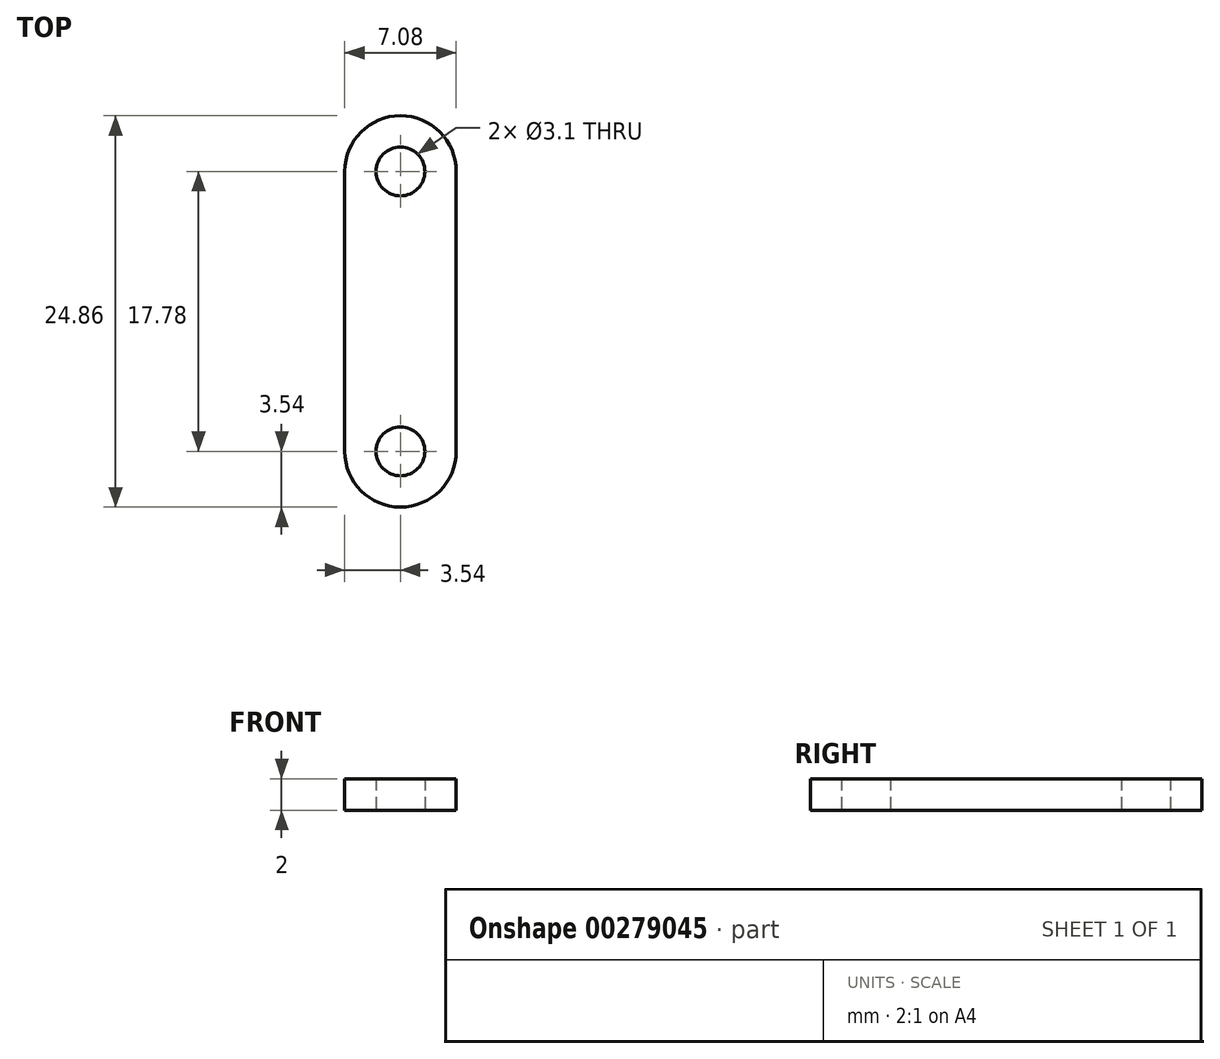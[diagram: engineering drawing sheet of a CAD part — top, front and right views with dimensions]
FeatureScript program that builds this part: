
annotation { "Feature Type Name" : "Feature", "Feature Type Description" : "" }
export const myFeature = defineFeature(function(context is Context, id is Id, definition is map)
    precondition{}
    {
        {
            var Q0;
            Q0=qCreatedBy(makeId("Top.planeOp"),FACE);
            var sketch = newSketch(context, id + "F0", { "sketchPlane" : qUnion([Q0])});
            skLineSegment(sketch, "E0.bottom", {"start": v(0, -12.43) * mm, "end": v(0, -12.43) * mm});
            skLineSegment(sketch, "E0.top", {"start": v(0, 12.43) * mm, "end": v(0, 12.43) * mm});
            skLineSegment(sketch, "E0.left", {"start": v(3.54, -8.9) * mm, "end": v(3.54, 8.9) * mm});
            skLineSegment(sketch, "E0.right", {"start": v(-3.54, -8.89) * mm, "end": v(-3.54, 8.89) * mm});
            skPoint(sketch, "E0.middle", {"position": v(0, 0) * mm});
            skLineSegment(sketch, "E1", {"start": v(-7.16, -8.9) * mm, "end": v(6.8, -8.9) * mm, "construction": true});
            skLineSegment(sketch, "E2", {"start": v(-9.41, 8.9) * mm, "end": v(8.22, 8.9) * mm, "construction": true});
            skCircle(sketch, "E3", {"center": v(0, 8.9) * mm, "radius": 1.55 * mm});
            skCircle(sketch, "E4", {"center": v(0, -8.9) * mm, "radius": 1.55 * mm});
            skPoint(sketch, "E4.centerSnap0", {"position": v(0, -12.43) * mm});
            skPoint(sketch, "E5.visualSharp", {"position": v(3.54, -12.43) * mm});
            skArc(sketch, "E5.filletArc", {"start": v(0, -12.43) * mm, "mid": v(2.5, -11.4) * mm, "end": v(3.54, -8.9) * mm});
            skPoint(sketch, "E6.visualSharp", {"position": v(-3.54, -12.43) * mm});
            skArc(sketch, "E6.filletArc", {"start": v(-3.25, -10.3) * mm, "mid": v(-1.94, -11.85) * mm, "end": v(0, -12.43) * mm});
            skPoint(sketch, "E7.visualSharp", {"position": v(-3.54, -8.9) * mm});
            skArc(sketch, "E7.filletArc", {"start": v(-3.54, -8.89) * mm, "mid": v(-3.47, -9.6) * mm, "end": v(-3.25, -10.3) * mm});
            skPoint(sketch, "E8.visualSharp", {"position": v(-3.54, 12.43) * mm});
            skArc(sketch, "E8.filletArc", {"start": v(0, 12.43) * mm, "mid": v(-2.5, 11.4) * mm, "end": v(-3.54, 8.89) * mm});
            skPoint(sketch, "E9.visualSharp", {"position": v(3.54, 12.43) * mm});
            skArc(sketch, "E9.filletArc", {"start": v(3.54, 8.9) * mm, "mid": v(2.5, 11.4) * mm, "end": v(0, 12.43) * mm});
            skSolve(sketch);
        }
        {
            var Q0;
            Q0=makeQuery(id+"F0.imprint","IMPRINT",FACE,{"disambiguationData":[TD([[makeQuery(id+"F0.imprint","IMPRINT",EDGE,{"derivedFrom":sQuery(id+"F0.wireOp",EDGE,"E0.left")}),1.0]])]});
            extrude(context, id + "F1", {"entities" : qUnion([Q0]), "depth" : 2 * mm});
        }
    });
